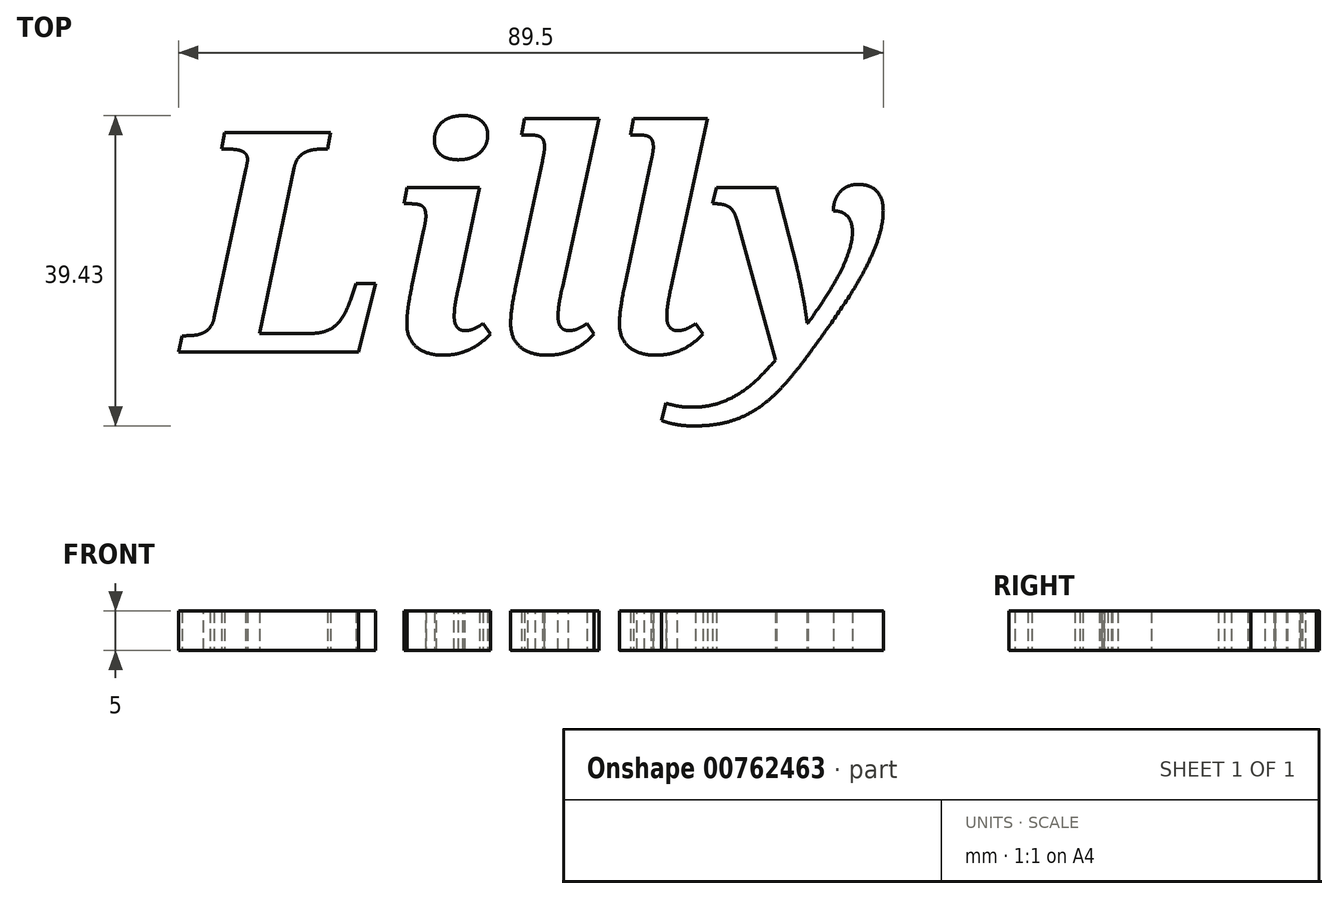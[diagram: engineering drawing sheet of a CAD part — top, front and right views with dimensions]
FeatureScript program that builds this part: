
annotation { "Feature Type Name" : "Feature", "Feature Type Description" : "" }
export const myFeature = defineFeature(function(context is Context, id is Id, definition is map)
    precondition{}
    {
        {
            var Q0;
            Q0=qCreatedBy(makeId("Top.planeOp"),FACE);
            var sketch = newSketch(context, id + "F0", { "sketchPlane" : qUnion([Q0])});
            skText(sketch, "E0", { "text": "Lilly", "fontName": "NotoSerif-BoldItalic.ttf"});
            const initialGuessF0  = {"E0": [-0.03753, 0.00184, 1, 0, 0.0281]};
            skSetInitialGuess(sketch, initialGuessF0);
            skSolve(sketch);
        }
        {
            var Q0;
            Q0 = qSketchRegion(id + "F0", true);
            extrude(context, id + "F1", {"entities" : qUnion([Q0]), "depth" : 5 * mm, "offsetDistance" : 25 * mm});
        }
    });
